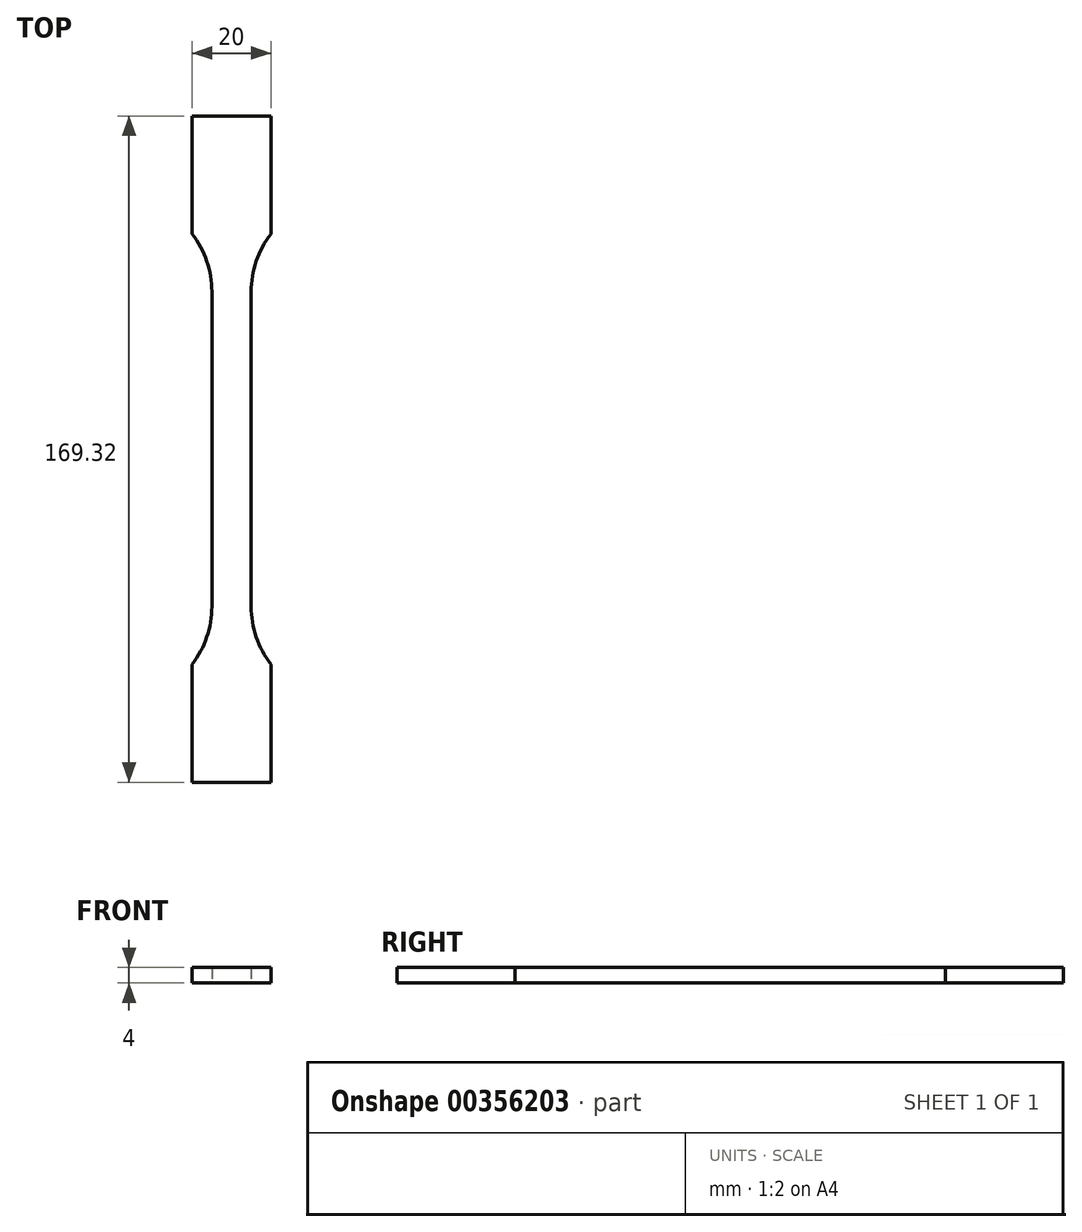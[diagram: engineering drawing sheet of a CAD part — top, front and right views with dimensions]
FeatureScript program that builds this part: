
annotation { "Feature Type Name" : "Feature", "Feature Type Description" : "" }
export const myFeature = defineFeature(function(context is Context, id is Id, definition is map)
    precondition{}
    {
        {
            var Q0;
            Q0=qCreatedBy(makeId("Top.planeOp"),FACE);
            var sketch = newSketch(context, id + "F0", { "sketchPlane" : qUnion([Q0])});
            skLineSegment(sketch, "E0", {"start": v(-5, 0) * mm, "end": v(-5, 40) * mm});
            skLineSegment(sketch, "E1", {"start": v(-10, 54.66) * mm, "end": v(-10, 84.66) * mm});
            skLineSegment(sketch, "E2", {"start": v(-10, 84.66) * mm, "end": v(0, 84.66) * mm});
            skLineSegment(sketch, "E3", {"start": v(0, 84.66) * mm, "end": v(0, 0) * mm});
            skLineSegment(sketch, "E4", {"start": v(0, 0) * mm, "end": v(-5, 0) * mm});
            skArc(sketch, "E5", {"start": v(-5, 40) * mm, "mid": v(-6.28, 47.75) * mm, "end": v(-10, 54.66) * mm});
            skSolve(sketch);
        }
        {
            var Q0;
            Q0=qSketchRegion(id+"F0",true);
            extrude(context, id + "F1", {"entities" : qUnion([Q0]), "depth" : 4 * mm});
        }
        {
            var Q0;
            Q0=makeQuery(id+"F1.opExtrude","SWEPT_BODY",BODY,{"disambiguationData":[OSD([sQuery(id+"F0.wireOp",EDGE,"E0"),sQuery(id+"F0.wireOp",EDGE,"E1"),sQuery(id+"F0.wireOp",EDGE,"E2"),sQuery(id+"F0.wireOp",EDGE,"E3"),sQuery(id+"F0.wireOp",EDGE,"E4"),sQuery(id+"F0.wireOp",EDGE,"E5")])]});
            var Q1;
            Q1=makeQuery(id+"F1.opExtrude","SWEPT_FACE",FACE,{"disambiguationData":[OSD([sQuery(id+"F0.wireOp",EDGE,"E3")])]});
            mirror(context, id + "F2", {"operationType" : NewBodyOperationType.ADD, "entities" : qUnion([Q0]), "mirrorPlane" : qUnion([Q1])});
        }
        {
            var Q0;
            Q0=makeQuery(id+"F1.opExtrude","SWEPT_BODY",BODY,{"disambiguationData":[OSD([sQuery(id+"F0.wireOp",EDGE,"E0"),sQuery(id+"F0.wireOp",EDGE,"E1"),sQuery(id+"F0.wireOp",EDGE,"E2"),sQuery(id+"F0.wireOp",EDGE,"E3"),sQuery(id+"F0.wireOp",EDGE,"E4"),sQuery(id+"F0.wireOp",EDGE,"E5")])]});
            var Q1;
            {var subQ0=makeQuery(id+"F1.opExtrude","SWEPT_FACE",FACE,{"disambiguationData":[OSD([sQuery(id+"F0.wireOp",EDGE,"E4")])]});Q1=makeQuery(id+"F2.boolean.opBoolean","MERGE",FACE,{"derivedFrom":[subQ0,makeQuery(id+"F2.opPattern","COPY",FACE,{"derivedFrom":subQ0,"instanceName":"1"})]});}
            mirror(context, id + "F3", {"operationType" : NewBodyOperationType.ADD, "entities" : qUnion([Q0]), "mirrorPlane" : qUnion([Q1])});
        }
    });
